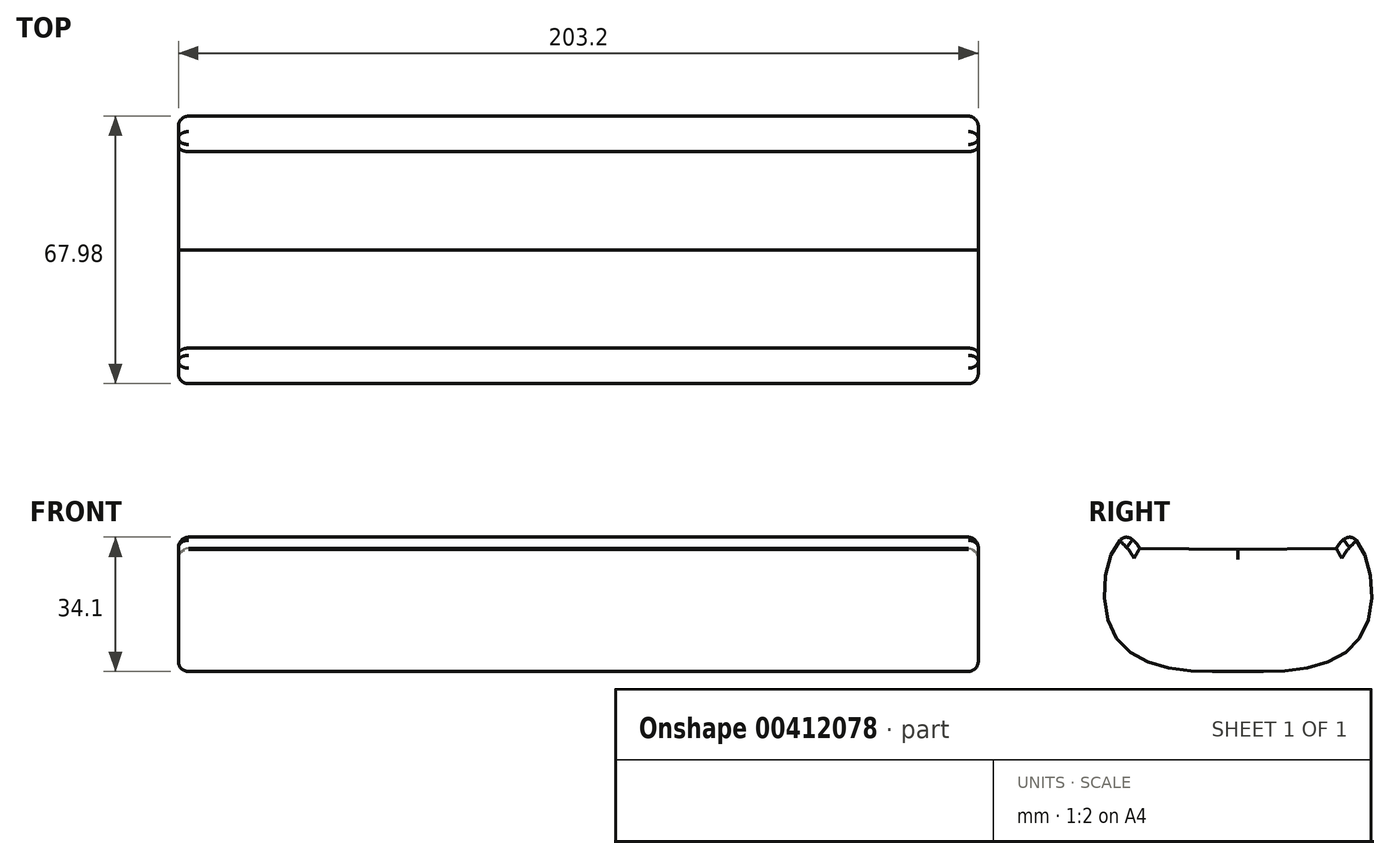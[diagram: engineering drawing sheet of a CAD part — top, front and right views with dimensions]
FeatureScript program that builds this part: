
annotation { "Feature Type Name" : "Feature", "Feature Type Description" : "" }
export const myFeature = defineFeature(function(context is Context, id is Id, definition is map)
    precondition{}
    {
        {
            var Q0;
            Q0=qCreatedBy(makeId("Right.planeOp"),FACE);
            cPlane(context, id + "F0", {"entities" : qUnion([Q0]), "cplaneType" : CPlaneType.OFFSET, "offset" : 101.6 * mm, "oppositeDirection" : true, "width" : 152.4 * mm, "height" : 152.4 * mm});
        }
        {
            var Q0;
            Q0=qCreatedBy(makeId("Right.planeOp"),FACE);
            cPlane(context, id + "F1", {"entities" : qUnion([Q0]), "cplaneType" : CPlaneType.OFFSET, "offset" : 50.8 * mm, "oppositeDirection" : true, "width" : 152.4 * mm, "height" : 152.4 * mm});
        }
        {
            var Q0;
            Q0=qCreatedBy(makeId("Right.planeOp"),FACE);
            cPlane(context, id + "F2", {"entities" : qUnion([Q0]), "cplaneType" : CPlaneType.OFFSET, "offset" : 50.8 * mm, "width" : 152.4 * mm, "height" : 152.4 * mm});
        }
        {
            var Q0;
            Q0=qCreatedBy(makeId("Right.planeOp"),FACE);
            cPlane(context, id + "F3", {"entities" : qUnion([Q0]), "cplaneType" : CPlaneType.OFFSET, "offset" : 101.6 * mm, "width" : 152.4 * mm, "height" : 152.4 * mm});
        }
        {
            var Q0;
            Q0=qCreatedBy(id+"F0.planeOp",FACE);
            var sketch = newSketch(context, id + "F4", { "sketchPlane" : qUnion([Q0])});
            skFitSpline(sketch, "E0", {"points": [v(0, 10.82) * mm, v(-24.96, 11.11) * mm], "startDerivative": vector(-24.96, 0.3) * mm, "endDerivative": vector(-24.96, 0.3) * mm});
            skFitSpline(sketch, "E1", {"points": [v(-24.96, 11.11) * mm, v(-31.5, 11.11) * mm, v(-32.39, -9.1) * mm, v(-18.12, -19.2) * mm, v(0, -20.08) * mm], "startDerivative": vector(-51.64, 82.63) * mm, "endDerivative": vector(42.15, 0) * mm});
            skLineSegment(sketch, "E2", {"start": v(0, 1.3) * mm, "end": v(0, -14.74) * mm});
            skFitSpline(sketch, "E3.MirrorCS", {"points": [v(24.96, 11.11) * mm, v(31.5, 11.11) * mm, v(32.39, -9.1) * mm, v(18.12, -19.2) * mm, v(0, -20.08) * mm], "startDerivative": vector(51.64, 82.63) * mm, "endDerivative": vector(-42.15, 0) * mm});
            skFitSpline(sketch, "E4.MirrorCS", {"points": [v(0, 10.82) * mm, v(24.96, 11.11) * mm], "startDerivative": vector(24.96, 0.3) * mm, "endDerivative": vector(24.96, 0.3) * mm});
            skSolve(sketch);
        }
        {
            var Q0;
            Q0=qCreatedBy(id+"F1.planeOp",FACE);
            var sketch = newSketch(context, id + "F5", { "sketchPlane" : qUnion([Q0])});
            skFitSpline(sketch, "E5", {"points": [v(0, 10.82) * mm, v(-24.96, 11.11) * mm], "startDerivative": vector(-24.96, 0.3) * mm, "endDerivative": vector(-24.96, 0.3) * mm});
            skFitSpline(sketch, "E6", {"points": [v(-24.96, 11.11) * mm, v(-31.5, 11.11) * mm, v(-32.39, -9.1) * mm, v(-18.12, -19.2) * mm, v(0, -20.08) * mm], "startDerivative": vector(-51.64, 82.63) * mm, "endDerivative": vector(42.15, 0) * mm});
            skLineSegment(sketch, "E7", {"start": v(0, 1.3) * mm, "end": v(0, -14.74) * mm});
            skFitSpline(sketch, "E8.MirrorCS", {"points": [v(24.96, 11.11) * mm, v(31.5, 11.11) * mm, v(32.39, -9.1) * mm, v(18.12, -19.2) * mm, v(0, -20.08) * mm], "startDerivative": vector(51.64, 82.63) * mm, "endDerivative": vector(-42.15, 0) * mm});
            skFitSpline(sketch, "E9.MirrorCS", {"points": [v(0, 10.82) * mm, v(24.96, 11.11) * mm], "startDerivative": vector(24.96, 0.3) * mm, "endDerivative": vector(24.96, 0.3) * mm});
            skSolve(sketch);
        }
        {
            var Q0;
            Q0=qCreatedBy(makeId("Right.planeOp"),FACE);
            var sketch = newSketch(context, id + "F6", { "sketchPlane" : qUnion([Q0])});
            skFitSpline(sketch, "E10", {"points": [v(0, 10.82) * mm, v(-24.96, 11.11) * mm], "startDerivative": vector(-24.96, 0.3) * mm, "endDerivative": vector(-24.96, 0.3) * mm});
            skFitSpline(sketch, "E11", {"points": [v(-24.96, 11.11) * mm, v(-31.5, 11.11) * mm, v(-32.39, -9.1) * mm, v(-18.12, -19.2) * mm, v(0, -20.08) * mm], "startDerivative": vector(-51.64, 82.63) * mm, "endDerivative": vector(42.15, 0) * mm});
            skLineSegment(sketch, "E12", {"start": v(0, 1.3) * mm, "end": v(0, -14.74) * mm});
            skFitSpline(sketch, "E13.MirrorCS", {"points": [v(24.96, 11.11) * mm, v(31.5, 11.11) * mm, v(32.39, -9.1) * mm, v(18.12, -19.2) * mm, v(0, -20.08) * mm], "startDerivative": vector(51.64, 82.63) * mm, "endDerivative": vector(-42.15, 0) * mm});
            skFitSpline(sketch, "E14.MirrorCS", {"points": [v(0, 10.82) * mm, v(24.96, 11.11) * mm], "startDerivative": vector(24.96, 0.3) * mm, "endDerivative": vector(24.96, 0.3) * mm});
            skSolve(sketch);
        }
        {
            var Q0;
            Q0=qCreatedBy(id+"F2.planeOp",FACE);
            var sketch = newSketch(context, id + "F7", { "sketchPlane" : qUnion([Q0])});
            skFitSpline(sketch, "E15", {"points": [v(0, 10.82) * mm, v(-24.96, 11.11) * mm], "startDerivative": vector(-24.96, 0.3) * mm, "endDerivative": vector(-24.96, 0.3) * mm});
            skFitSpline(sketch, "E16", {"points": [v(-24.96, 11.11) * mm, v(-31.5, 11.11) * mm, v(-32.39, -9.1) * mm, v(-18.12, -19.2) * mm, v(0, -20.08) * mm], "startDerivative": vector(-51.64, 82.63) * mm, "endDerivative": vector(42.15, 0) * mm});
            skLineSegment(sketch, "E17", {"start": v(0, 1.3) * mm, "end": v(0, -14.74) * mm});
            skFitSpline(sketch, "E18.MirrorCS", {"points": [v(24.96, 11.11) * mm, v(31.5, 11.11) * mm, v(32.39, -9.1) * mm, v(18.12, -19.2) * mm, v(0, -20.08) * mm], "startDerivative": vector(51.64, 82.63) * mm, "endDerivative": vector(-42.15, 0) * mm});
            skFitSpline(sketch, "E19.MirrorCS", {"points": [v(0, 10.82) * mm, v(24.96, 11.11) * mm], "startDerivative": vector(24.96, 0.3) * mm, "endDerivative": vector(24.96, 0.3) * mm});
            skSolve(sketch);
        }
        {
            var Q0;
            Q0=qCreatedBy(id+"F3.planeOp",FACE);
            var sketch = newSketch(context, id + "F8", { "sketchPlane" : qUnion([Q0])});
            skFitSpline(sketch, "E20", {"points": [v(0, 10.82) * mm, v(-24.96, 11.11) * mm], "startDerivative": vector(-24.96, 0.3) * mm, "endDerivative": vector(-24.96, 0.3) * mm});
            skFitSpline(sketch, "E21", {"points": [v(-24.96, 11.11) * mm, v(-31.5, 11.11) * mm, v(-32.39, -9.1) * mm, v(-18.12, -19.2) * mm, v(0, -20.08) * mm], "startDerivative": vector(-51.64, 82.63) * mm, "endDerivative": vector(42.15, 0) * mm});
            skLineSegment(sketch, "E22", {"start": v(0, 1.3) * mm, "end": v(0, -14.74) * mm});
            skFitSpline(sketch, "E23.MirrorCS", {"points": [v(24.96, 11.11) * mm, v(31.5, 11.11) * mm, v(32.39, -9.1) * mm, v(18.12, -19.2) * mm, v(0, -20.08) * mm], "startDerivative": vector(51.64, 82.63) * mm, "endDerivative": vector(-42.15, 0) * mm});
            skFitSpline(sketch, "E24.MirrorCS", {"points": [v(0, 10.82) * mm, v(24.96, 11.11) * mm], "startDerivative": vector(24.96, 0.3) * mm, "endDerivative": vector(24.96, 0.3) * mm});
            skSolve(sketch);
        }
        {
            var Q0;
            Q0=makeQuery(id+"F4.imprint","IMPRINT",FACE,{"disambiguationData":[TD([[makeQuery(id+"F4.imprint","IMPRINT",EDGE,{"derivedFrom":sQuery(id+"F4.wireOp",EDGE,"E0")}),1.0]])]});
            var Q1;
            Q1=makeQuery(id+"F5.imprint","IMPRINT",FACE,{"disambiguationData":[TD([[makeQuery(id+"F5.imprint","IMPRINT",EDGE,{"derivedFrom":sQuery(id+"F5.wireOp",EDGE,"E5")}),1.0]])]});
            var Q2;
            Q2=makeQuery(id+"F6.imprint","IMPRINT",FACE,{"disambiguationData":[TD([[makeQuery(id+"F6.imprint","IMPRINT",EDGE,{"derivedFrom":sQuery(id+"F6.wireOp",EDGE,"E10")}),1.0]])]});
            var Q3;
            Q3=makeQuery(id+"F7.imprint","IMPRINT",FACE,{"disambiguationData":[TD([[makeQuery(id+"F7.imprint","IMPRINT",EDGE,{"derivedFrom":sQuery(id+"F7.wireOp",EDGE,"E15")}),1.0]])]});
            var Q4;
            Q4=makeQuery(id+"F8.imprint","IMPRINT",FACE,{"disambiguationData":[TD([[makeQuery(id+"F8.imprint","IMPRINT",EDGE,{"derivedFrom":sQuery(id+"F8.wireOp",EDGE,"E20")}),1.0]])]});
            loft(context, id + "F9", {"sheetProfilesArray" : [{ "sheetProfileEntities" : qUnion([Q0]) }, { "sheetProfileEntities" : qUnion([Q1]) }, { "sheetProfileEntities" : qUnion([Q2]) }, { "sheetProfileEntities" : qUnion([Q3]) }, { "sheetProfileEntities" : qUnion([Q4]) }]});
        }
        {
            assignVariable(context, id + "F10", {"name" : "loftAmount", "anyValue" : 2.54 * mm});
        }
        {
            var Q0;
            Q0=makeQuery(id+"F9.opLoft","MID_CAP_EDGE",EDGE,{"disambiguationData":[OSD([sQuery(id+"F8.wireOp",EDGE,"E21"),sQuery(id+"F8.wireOp",EDGE,"E23.MirrorCS"),sQuery(id+"F8.wireOp",EDGE,"E24.MirrorCS")])],"capPos":4.0});
            var Q1;
            Q1=makeQuery(id+"F9.opLoft","MID_CAP_EDGE",EDGE,{"disambiguationData":[OSD([sQuery(id+"F8.wireOp",EDGE,"E20"),sQuery(id+"F8.wireOp",EDGE,"E23.MirrorCS"),sQuery(id+"F8.wireOp",EDGE,"E24.MirrorCS")])],"capPos":4.0});
            var Q2;
            Q2=makeQuery(id+"F9.opLoft","MID_CAP_EDGE",EDGE,{"disambiguationData":[OSD([sQuery(id+"F8.wireOp",EDGE,"E20"),sQuery(id+"F8.wireOp",EDGE,"E21"),sQuery(id+"F8.wireOp",EDGE,"E24.MirrorCS")])],"capPos":4.0});
            var Q3;
            Q3=makeQuery(id+"F9.opLoft","MID_CAP_EDGE",EDGE,{"disambiguationData":[OSD([sQuery(id+"F8.wireOp",EDGE,"E20"),sQuery(id+"F8.wireOp",EDGE,"E21"),sQuery(id+"F8.wireOp",EDGE,"E23.MirrorCS")])],"capPos":4.0});
            fillet(context, id + "F11", {"entities" : qUnion([Q0, Q1, Q2, Q3]), "radius" : getVariable(context, 'loftAmount'), "tangentPropagation" : true, "allowEdgeOverflow" : false});
        }
        {
            var Q0;
            Q0=makeQuery(id+"F9.opLoft","MID_CAP_EDGE",EDGE,{"disambiguationData":[OSD([sQuery(id+"F4.wireOp",EDGE,"E1"),sQuery(id+"F4.wireOp",EDGE,"E3.MirrorCS"),sQuery(id+"F4.wireOp",EDGE,"E4.MirrorCS")])],"capPos":0.0});
            var Q1;
            Q1=makeQuery(id+"F9.opLoft","MID_CAP_EDGE",EDGE,{"disambiguationData":[OSD([sQuery(id+"F4.wireOp",EDGE,"E0"),sQuery(id+"F4.wireOp",EDGE,"E3.MirrorCS"),sQuery(id+"F4.wireOp",EDGE,"E4.MirrorCS")])],"capPos":0.0});
            var Q2;
            Q2=makeQuery(id+"F9.opLoft","MID_CAP_EDGE",EDGE,{"disambiguationData":[OSD([sQuery(id+"F4.wireOp",EDGE,"E0"),sQuery(id+"F4.wireOp",EDGE,"E1"),sQuery(id+"F4.wireOp",EDGE,"E4.MirrorCS")])],"capPos":0.0});
            var Q3;
            Q3=makeQuery(id+"F9.opLoft","MID_CAP_EDGE",EDGE,{"disambiguationData":[OSD([sQuery(id+"F4.wireOp",EDGE,"E0"),sQuery(id+"F4.wireOp",EDGE,"E1"),sQuery(id+"F4.wireOp",EDGE,"E3.MirrorCS")])],"capPos":0.0});
            fillet(context, id + "F12", {"entities" : qUnion([Q0, Q1, Q2, Q3]), "radius" : getVariable(context, 'loftAmount'), "tangentPropagation" : true, "allowEdgeOverflow" : false});
        }
    });
